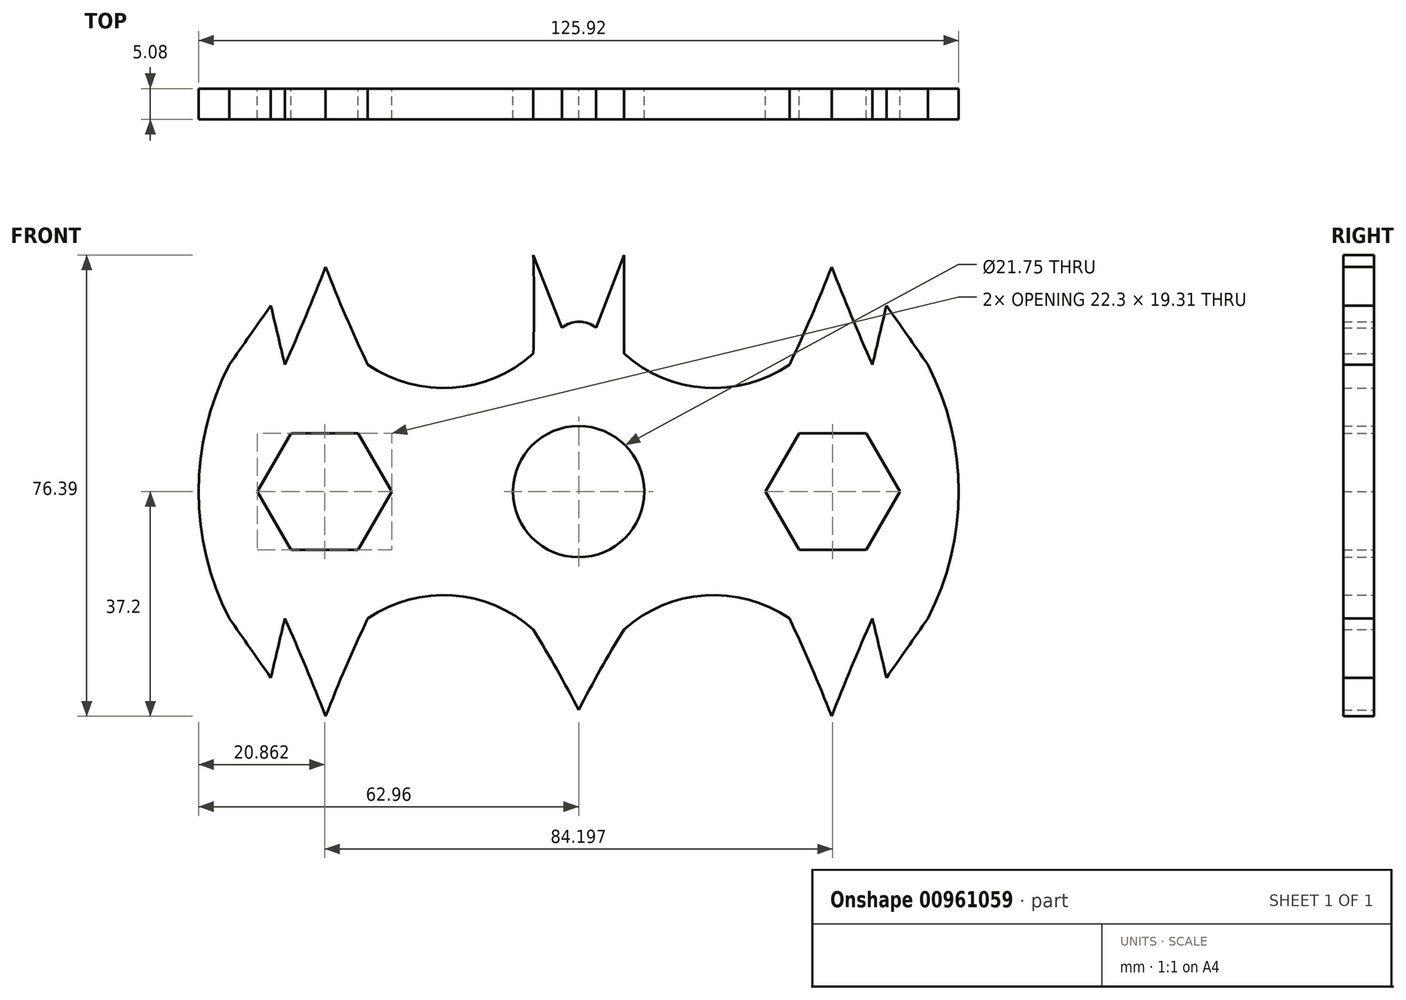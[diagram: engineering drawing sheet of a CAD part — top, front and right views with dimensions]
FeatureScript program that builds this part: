
annotation { "Feature Type Name" : "Feature", "Feature Type Description" : "" }
export const myFeature = defineFeature(function(context is Context, id is Id, definition is map)
    precondition{}
    {
        {
            var Q0;
            Q0=qCreatedBy(makeId("Front.planeOp"),FACE);
            var sketch = newSketch(context, id + "F0", { "sketchPlane" : qUnion([Q0])});
            skArc(sketch, "E0", {"start": v(0, -36.22) * mm, "mid": v(-3.61, -29.46) * mm, "end": v(-7.5, -22.86) * mm});
            skArc(sketch, "E1.MirrorCS", {"start": v(0, -36.22) * mm, "mid": v(3.61, -29.46) * mm, "end": v(7.5, -22.86) * mm});
            skArc(sketch, "E2", {"start": v(-7.5, -22.86) * mm, "mid": v(-20.9, -17.2) * mm, "end": v(-34.95, -21.02) * mm});
            skArc(sketch, "E3", {"start": v(-34.95, -21.02) * mm, "mid": v(-38.57, -29.05) * mm, "end": v(-41.93, -37.2) * mm});
            skArc(sketch, "E4", {"start": v(-41.93, -37.2) * mm, "mid": v(-45.2, -29.07) * mm, "end": v(-48.67, -21.02) * mm});
            skArc(sketch, "E5", {"start": v(-48.67, -21.02) * mm, "mid": v(-49.84, -25.92) * mm, "end": v(-51, -30.82) * mm});
            skArc(sketch, "E6", {"start": v(-57.86, -21.02) * mm, "mid": v(-54.44, -25.93) * mm, "end": v(-51, -30.82) * mm});
            skArc(sketch, "E7.MirrorCS", {"start": v(7.5, -22.86) * mm, "mid": v(20.9, -17.2) * mm, "end": v(34.95, -21.02) * mm});
            skArc(sketch, "E8.MirrorCS", {"start": v(34.95, -21.02) * mm, "mid": v(38.57, -29.05) * mm, "end": v(41.93, -37.2) * mm});
            skArc(sketch, "E9.MirrorCS", {"start": v(41.93, -37.2) * mm, "mid": v(45.2, -29.07) * mm, "end": v(48.67, -21.02) * mm});
            skArc(sketch, "E10.MirrorCS", {"start": v(48.67, -21.02) * mm, "mid": v(49.84, -25.92) * mm, "end": v(51, -30.82) * mm});
            skArc(sketch, "E11.MirrorCS", {"start": v(57.86, -21.02) * mm, "mid": v(54.44, -25.93) * mm, "end": v(51, -30.82) * mm});
            skArc(sketch, "E12.MirrorCS", {"start": v(-41.93, 37.2) * mm, "mid": v(-45.2, 29.07) * mm, "end": v(-48.67, 21.02) * mm});
            skArc(sketch, "E13.MirrorCS", {"start": v(-48.67, 21.02) * mm, "mid": v(-49.84, 25.92) * mm, "end": v(-51, 30.82) * mm});
            skArc(sketch, "E14.MirrorCS", {"start": v(-57.86, 21.02) * mm, "mid": v(-54.44, 25.93) * mm, "end": v(-51, 30.82) * mm});
            skArc(sketch, "E15.MirrorCS", {"start": v(-34.95, 21.02) * mm, "mid": v(-38.57, 29.05) * mm, "end": v(-41.93, 37.2) * mm});
            skArc(sketch, "E16.MirrorCS", {"start": v(-7.5, 22.86) * mm, "mid": v(-20.9, 17.2) * mm, "end": v(-34.95, 21.02) * mm});
            skArc(sketch, "E17.MirrorCS", {"start": v(7.5, 22.86) * mm, "mid": v(20.9, 17.2) * mm, "end": v(34.95, 21.02) * mm});
            skArc(sketch, "E18.MirrorCS", {"start": v(34.95, 21.02) * mm, "mid": v(38.57, 29.05) * mm, "end": v(41.93, 37.2) * mm});
            skArc(sketch, "E19.MirrorCS", {"start": v(41.93, 37.2) * mm, "mid": v(45.2, 29.07) * mm, "end": v(48.67, 21.02) * mm});
            skArc(sketch, "E20.MirrorCS", {"start": v(48.67, 21.02) * mm, "mid": v(49.84, 25.92) * mm, "end": v(51, 30.82) * mm});
            skArc(sketch, "E21.MirrorCS", {"start": v(57.86, 21.02) * mm, "mid": v(54.44, 25.93) * mm, "end": v(51, 30.82) * mm});
            skArc(sketch, "E22", {"start": v(-57.86, 21.02) * mm, "mid": v(-62.96, 0) * mm, "end": v(-57.86, -21.02) * mm});
            skArc(sketch, "E23.MirrorCS", {"start": v(57.86, 21.02) * mm, "mid": v(62.96, 0) * mm, "end": v(57.86, -21.02) * mm});
            skArc(sketch, "E24", {"start": v(-7.5, 22.86) * mm, "mid": v(-7.4, 31.03) * mm, "end": v(-7.5, 39.2) * mm});
            skLineSegment(sketch, "E25", {"start": v(-7.5, 39.2) * mm, "end": v(-2.77, 27.1) * mm});
            skLineSegment(sketch, "E26", {"start": v(7.5, 22.86) * mm, "end": v(7.5, 39.2) * mm});
            skLineSegment(sketch, "E27", {"start": v(7.5, 39.2) * mm, "end": v(2.9, 27.1) * mm});
            skArc(sketch, "E28", {"start": v(2.9, 27.1) * mm, "mid": v(0.07, 28.12) * mm, "end": v(-2.77, 27.1) * mm});
            skPoint(sketch, "E29.0.midPoint", {"position": v(-34.7, 10.1) * mm});
            skLineSegment(sketch, "E30.0", {"start": v(36.52, 9.66) * mm, "end": v(47.67, 9.66) * mm});
            skLineSegment(sketch, "E30.1", {"start": v(47.67, 9.66) * mm, "end": v(53.25, 0) * mm});
            skLineSegment(sketch, "E30.2", {"start": v(53.25, 0) * mm, "end": v(47.67, -9.66) * mm});
            skLineSegment(sketch, "E30.3", {"start": v(47.67, -9.66) * mm, "end": v(36.52, -9.66) * mm});
            skLineSegment(sketch, "E30.4", {"start": v(36.52, -9.66) * mm, "end": v(30.95, 0) * mm});
            skLineSegment(sketch, "E30.5", {"start": v(30.95, 0) * mm, "end": v(36.52, 9.66) * mm});
            skPoint(sketch, "E30.0.midPoint", {"position": v(42.1, 9.66) * mm});
            skLineSegment(sketch, "E31.MirrorCS", {"start": v(-36.52, 9.66) * mm, "end": v(-47.67, 9.66) * mm});
            skLineSegment(sketch, "E32.MirrorCS", {"start": v(-30.95, 0) * mm, "end": v(-36.52, 9.66) * mm});
            skLineSegment(sketch, "E33.MirrorCS", {"start": v(-36.52, -9.66) * mm, "end": v(-30.95, 0) * mm});
            skLineSegment(sketch, "E34.MirrorCS", {"start": v(-47.67, -9.66) * mm, "end": v(-36.52, -9.66) * mm});
            skLineSegment(sketch, "E35.MirrorCS", {"start": v(-53.25, 0) * mm, "end": v(-47.67, -9.66) * mm});
            skLineSegment(sketch, "E36.MirrorCS", {"start": v(-47.67, 9.66) * mm, "end": v(-53.25, 0) * mm});
            skCircle(sketch, "E37", {"center": v(0, 0) * mm, "radius": 10.87 * mm});
            skSolve(sketch);
        }
        {
            var Q0;
            Q0=qSketchRegion(id+"F0",true);
            extrude(context, id + "F1", {"entities" : qUnion([Q0]), "depth" : 5.08 * mm, "offsetDistance" : 25.4 * mm});
        }
    });
